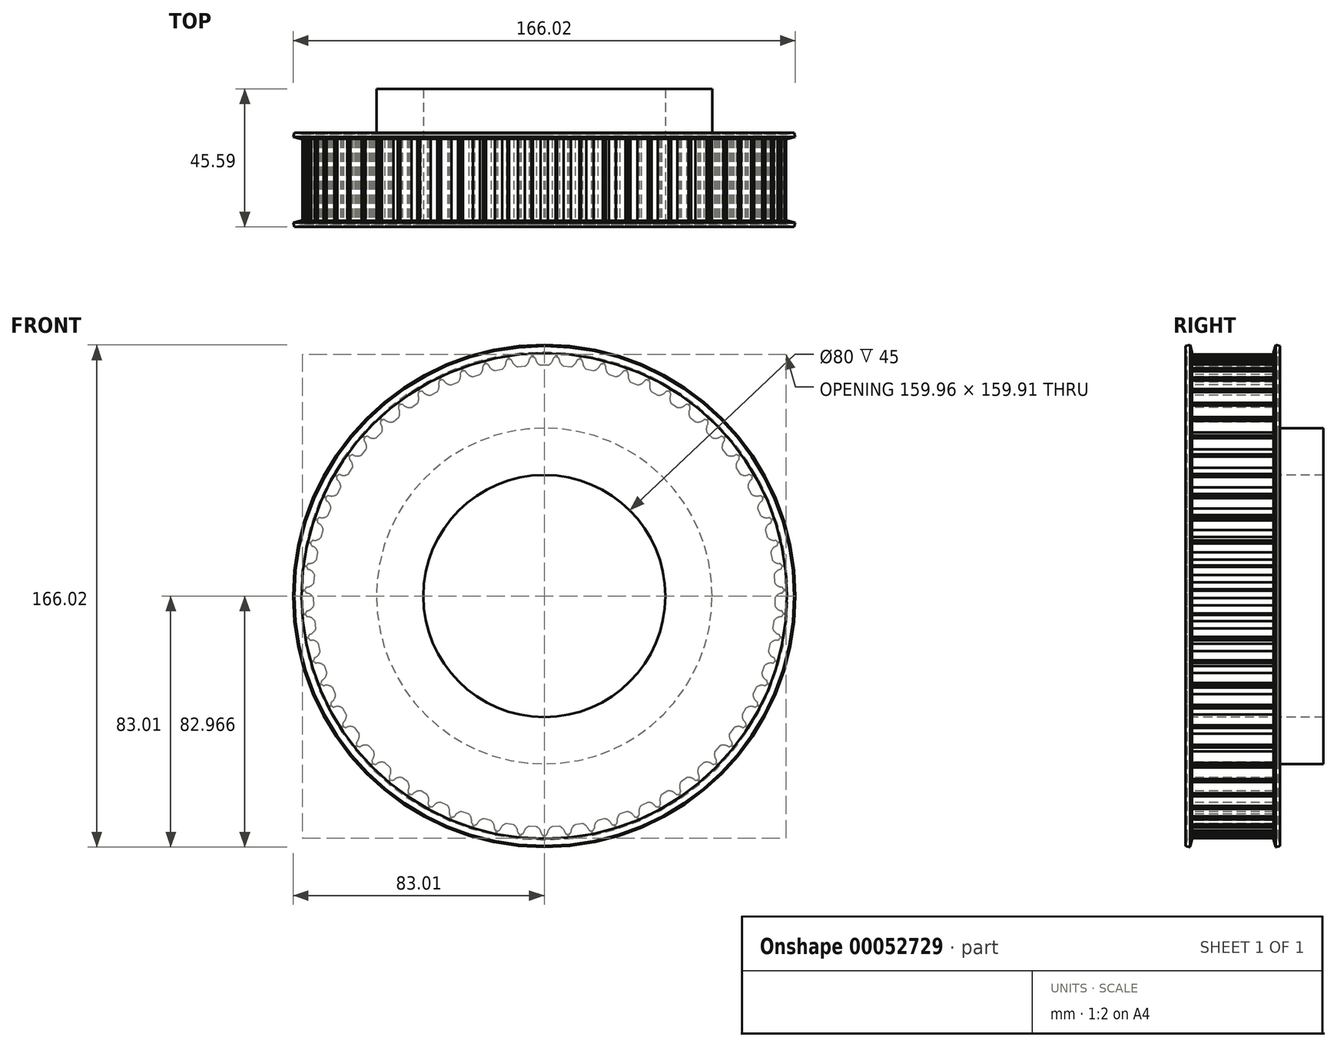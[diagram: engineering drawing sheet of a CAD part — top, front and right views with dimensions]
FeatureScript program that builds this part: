
annotation { "Feature Type Name" : "Feature", "Feature Type Description" : "" }
export const myFeature = defineFeature(function(context is Context, id is Id, definition is map)
    precondition{}
    {
        {
            var Q0;
            Q0=qCreatedBy(makeId("Right.planeOp"),FACE);
            var sketch = newSketch(context, id + "F0", { "sketchPlane" : qUnion([Q0])});
            skLineSegment(sketch, "E0", {"start": v(-51.89, 0) * mm, "end": v(51.76, 0) * mm, "construction": true});
            skLineSegment(sketch, "E1", {"start": v(0, 40) * mm, "end": v(0, 80) * mm});
            skLineSegment(sketch, "E2", {"start": v(0, 80) * mm, "end": v(30, 80) * mm});
            skLineSegment(sketch, "E3", {"start": v(30, 80) * mm, "end": v(30, 55.5) * mm});
            skLineSegment(sketch, "E4", {"start": v(30, 55.5) * mm, "end": v(45, 55.5) * mm});
            skLineSegment(sketch, "E5", {"start": v(45, 55.5) * mm, "end": v(45, 40) * mm});
            skLineSegment(sketch, "E6", {"start": v(45, 40) * mm, "end": v(0, 40) * mm});
            skSolve(sketch);
        }
        {
            var Q0;
            Q0=makeQuery(id+"F0.imprint","IMPRINT",FACE,{"disambiguationData":[TD([[makeQuery(id+"F0.imprint","IMPRINT",EDGE,{"derivedFrom":sQuery(id+"F0.wireOp",EDGE,"E1")}),-1.0]])]});
            var Q1;
            Q1=sQuery(id+"F0.wireOp",EDGE,"E0");
            revolve(context, id + "F1", {"entities" : qUnion([Q0]), "axis" : qUnion([Q1]), "revolveType" : RevolveType.FULL});
        }
        {
            var Q0;
            Q0=makeQuery(id+"F1.opRevolve","SWEPT_FACE",FACE,{"disambiguationData":[OSD([sQuery(id+"F0.wireOp",EDGE,"E1")])]});
            var sketch = newSketch(context, id + "F2", { "sketchPlane" : qUnion([Q0])});
            skArc(sketch, "E7", {"start": v(-2.94, 78.4) * mm, "mid": v(0, 76) * mm, "end": v(2.94, 78.4) * mm});
            skLineSegment(sketch, "E8.rect.bottom", {"start": v(-3.75, 81) * mm, "end": v(3.75, 81) * mm});
            skLineSegment(sketch, "E8.rect.top", {"start": v(-3.75, 79) * mm, "end": v(-3.67, 79) * mm});
            skLineSegment(sketch, "E8.rect.left", {"start": v(-3.75, 81) * mm, "end": v(-3.75, 79) * mm});
            skLineSegment(sketch, "E8.rect.right", {"start": v(3.75, 81) * mm, "end": v(3.75, 79) * mm});
            skPoint(sketch, "E8.rect.middle", {"position": v(0, 80) * mm});
            skLineSegment(sketch, "E9.trimOffspring", {"start": v(3.67, 79) * mm, "end": v(3.75, 79) * mm});
            skPoint(sketch, "E10.visualSharp", {"position": v(-3, 79) * mm});
            skArc(sketch, "E10.filletArc", {"start": v(-2.94, 78.4) * mm, "mid": v(-3.2, 78.83) * mm, "end": v(-3.67, 79) * mm});
            skPoint(sketch, "E11.visualSharp", {"position": v(3, 79) * mm});
            skArc(sketch, "E11.filletArc", {"start": v(3.67, 79) * mm, "mid": v(3.2, 78.83) * mm, "end": v(2.94, 78.4) * mm});
            skLineSegment(sketch, "E12", {"start": v(-1.2, 76.25) * mm, "end": v(1.2, 76.25) * mm});
            skPoint(sketch, "E13", {"position": v(0, 76.25) * mm});
            skSolve(sketch);
        }
        {
            var Q0;
            {var subQ0=sQuery(id+"F2.wireOp",EDGE,"E8.rect.bottom");Q0=makeQuery(id+"F2.imprint","IMPRINT",FACE,{"disambiguationData":[TD([[makeQuery(id+"F2.imprint","IMPRINT",EDGE,{"derivedFrom":subQ0}),-1.0]])]});}
            var Q1;
            Q1=makeQuery(id+"F2.imprint","IMPRINT",FACE,{"disambiguationData":[TD([[makeQuery(id+"F2.imprint","IMPRINT",EDGE,{"derivedFrom":sQuery(id+"F2.wireOp",EDGE,"E7")}),1.0]])]});
            var Q2;
            Q2=makeQuery(id+"F1.opRevolve","SWEPT_FACE",FACE,{"disambiguationData":[OSD([sQuery(id+"F0.wireOp",EDGE,"E3")])]});
            extrude(context, id + "F3", {"entities" : qUnion([Q0, Q1]), "endBound" : BoundingType.THROUGH_ALL, "oppositeDirection" : true, "endBoundEntityFace" : qUnion([Q2]), "depth" : 25 * mm});
        }
        {
            var Q0;
            Q0=makeQuery(id+"F3.opExtrude","SWEPT_BODY",BODY,{"disambiguationData":[OSD([sQuery(id+"F2.wireOp",EDGE,"E7"),sQuery(id+"F2.wireOp",EDGE,"E8.rect.bottom"),sQuery(id+"F2.wireOp",EDGE,"E8.rect.top"),sQuery(id+"F2.wireOp",EDGE,"E8.rect.left"),sQuery(id+"F2.wireOp",EDGE,"E8.rect.right"),sQuery(id+"F2.wireOp",EDGE,"E9.trimOffspring"),sQuery(id+"F2.wireOp",EDGE,"E10.filletArc"),sQuery(id+"F2.wireOp",EDGE,"E11.filletArc"),sQuery(id+"F2.wireOp",EDGE,"E12")])]});
            var Q1;
            Q1=sQuery(id+"F0.wireOp",EDGE,"E0");
            circularPattern(context, id + "F4", {"operationType" : NewBodyOperationType.REMOVE, "entities" : qUnion([Q0]), "axis" : qUnion([Q1]), "angle" : 360 * degree, "instanceCount" : 63, "equalSpace" : true});
        }
        {
            var Q0;
            Q0=qCreatedBy(makeId("Right.planeOp"),FACE);
            var sketch = newSketch(context, id + "F5", { "sketchPlane" : qUnion([Q0])});
            skLineSegment(sketch, "E14", {"start": v(0, 0) * mm, "end": v(15, 0) * mm, "construction": true});
            skLineSegment(sketch, "E15", {"start": v(15, 0) * mm, "end": v(15, -79.13) * mm, "construction": true});
            skLineSegment(sketch, "E16", {"start": v(0, 76.25) * mm, "end": v(1.5, 76.25) * mm});
            skLineSegment(sketch, "E17", {"start": v(0, 76.25) * mm, "end": v(0, 80.61) * mm});
            skLineSegment(sketch, "E18", {"start": v(0, 80.61) * mm, "end": v(1.5, 80.61) * mm});
            skLineSegment(sketch, "E19", {"start": v(1.5, 80.61) * mm, "end": v(1.5, 76.25) * mm});
            skLineSegment(sketch, "E20", {"start": v(1.5, 80.61) * mm, "end": v(0.86, 83.01) * mm});
            skLineSegment(sketch, "E21", {"start": v(1.5, 80.61) * mm, "end": v(0, 80.21) * mm});
            skLineSegment(sketch, "E22", {"start": v(0.86, 83.01) * mm, "end": v(-0.6, 82.62) * mm});
            skLineSegment(sketch, "E23", {"start": v(-0.6, 82.62) * mm, "end": v(0, 80.21) * mm});
            skLineSegment(sketch, "E24", {"start": v(15, 0) * mm, "end": v(15, 84.63) * mm, "construction": true});
            skLineSegment(sketch, "E25.MirrorCS", {"start": v(30, 80.61) * mm, "end": v(28.5, 80.61) * mm});
            skLineSegment(sketch, "E26.MirrorCS", {"start": v(28.5, 80.61) * mm, "end": v(30, 80.21) * mm});
            skLineSegment(sketch, "E27.MirrorCS", {"start": v(30.6, 82.62) * mm, "end": v(30, 80.21) * mm});
            skLineSegment(sketch, "E28.MirrorCS", {"start": v(29.14, 83.01) * mm, "end": v(30.6, 82.62) * mm});
            skLineSegment(sketch, "E29.MirrorCS", {"start": v(30, 76.25) * mm, "end": v(28.5, 76.25) * mm});
            skLineSegment(sketch, "E30.MirrorCS", {"start": v(28.5, 80.61) * mm, "end": v(29.14, 83.01) * mm});
            skLineSegment(sketch, "E31.MirrorCS", {"start": v(30, 76.25) * mm, "end": v(30, 80.61) * mm});
            skLineSegment(sketch, "E32.MirrorCS", {"start": v(28.5, 80.61) * mm, "end": v(28.5, 76.25) * mm});
            skSolve(sketch);
        }
        {
            var Q0;
            {var subQ1=sQuery(id+"F5.wireOp",EDGE,"E18");Q0=makeQuery(id+"F5.imprint","IMPRINT",FACE,{"disambiguationData":[TD([[makeQuery(id+"F5.imprint","IMPRINT",EDGE,{"derivedFrom":subQ1}),1.0]])]});}
            var Q1;
            {var subQ0=sQuery(id+"F5.wireOp",EDGE,"E18");Q1=makeQuery(id+"F5.imprint","IMPRINT",FACE,{"disambiguationData":[TD([[makeQuery(id+"F5.imprint","IMPRINT",EDGE,{"derivedFrom":subQ0}),-1.0]])]});}
            var Q2;
            {var subQ0=sQuery(id+"F5.wireOp",EDGE,"E16");Q2=makeQuery(id+"F5.imprint","IMPRINT",FACE,{"disambiguationData":[TD([[makeQuery(id+"F5.imprint","IMPRINT",EDGE,{"derivedFrom":subQ0}),1.0]])]});}
            var Q3;
            {var subQ1=sQuery(id+"F5.wireOp",EDGE,"E25.MirrorCS");Q3=makeQuery(id+"F5.imprint","IMPRINT",FACE,{"disambiguationData":[TD([[makeQuery(id+"F5.imprint","IMPRINT",EDGE,{"derivedFrom":subQ1}),-1.0]])]});}
            var Q4;
            {var subQ0=sQuery(id+"F5.wireOp",EDGE,"E25.MirrorCS");Q4=makeQuery(id+"F5.imprint","IMPRINT",FACE,{"disambiguationData":[TD([[makeQuery(id+"F5.imprint","IMPRINT",EDGE,{"derivedFrom":subQ0}),1.0]])]});}
            var Q5;
            {var subQ0=sQuery(id+"F5.wireOp",EDGE,"E26.MirrorCS");Q5=makeQuery(id+"F5.imprint","IMPRINT",FACE,{"disambiguationData":[TD([[makeQuery(id+"F5.imprint","IMPRINT",EDGE,{"derivedFrom":subQ0}),-1.0]])]});}
            var Q6;
            Q6=sQuery(id+"F0.wireOp",EDGE,"E0");
            revolve(context, id + "F6", {"operationType" : NewBodyOperationType.ADD, "entities" : qUnion([Q0, Q1, Q2, Q3, Q4, Q5]), "axis" : qUnion([Q6]), "revolveType" : RevolveType.FULL});
        }
    });
